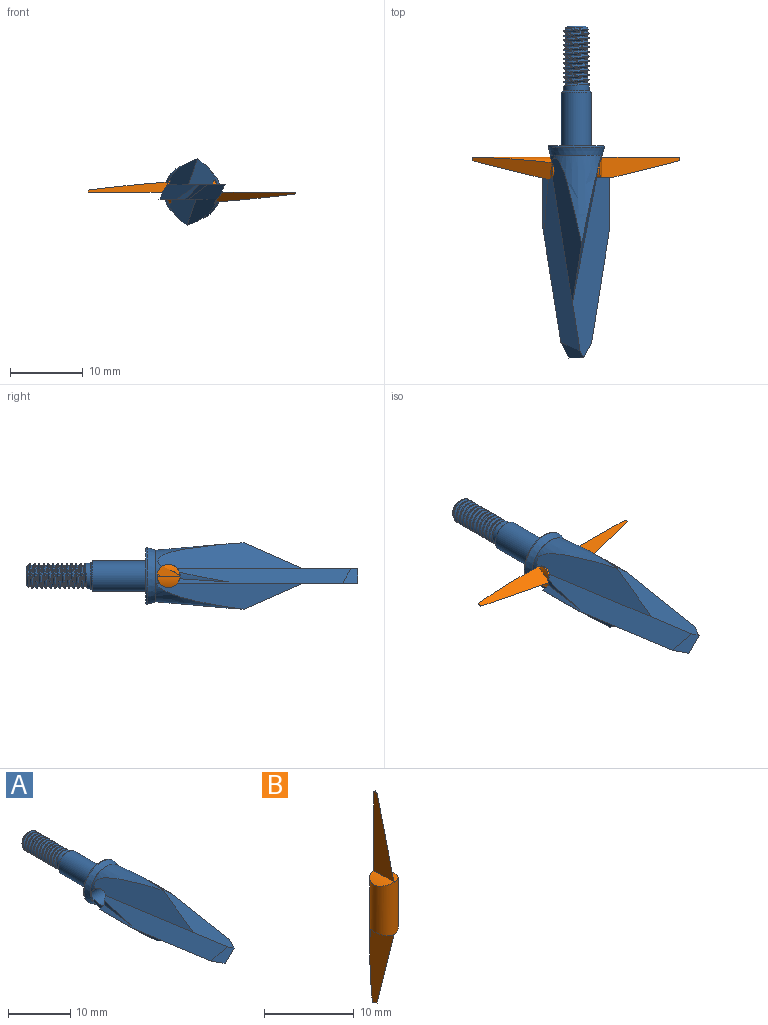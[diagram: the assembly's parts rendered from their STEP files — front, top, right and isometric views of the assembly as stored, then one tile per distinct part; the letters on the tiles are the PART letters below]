
ASSEMBLY  parts=2 mates=1
PART A: 55 faces, bbox 9.9x277.6x9.9 mm
  f0: plane 7.09x0.01mm, normal (-1,0,0), area 0.1mm2, adj f1,f2,f8,f33
  f1: plane 7.06x0.78mm, normal (-0.64,0,0.77), area 4.4mm2, adj f0,f2,f3,f33
  f2: cylinder r=1.59mm len=9.18mm, axis (-1,0,0), area 67.2mm2, adj f0,f1,f3,f4,f8,f9,f10,f11
  f3: cone r=3.56mm half-angle=5deg, axis (0,-1,0), area 3.2mm2, adj f1,f2,f33
  f4: plane 19.93x4.12mm, normal (0.81,-0.13,-0.57), area 58.8mm2, adj f2,f13,f26,f27,f28,f29,f32,f53
  f5: cylinder r=2.08mm len=7.37mm, axis (0,-1,0), area 96.4mm2, adj f7,f19
  f6: plane 3.66x3.66mm, normal (0,1,0), area 0.9mm2, adj f7,f34
  f7: cone r=1.83mm half-angle=45deg, axis (0,-1,0), area 4.4mm2, adj f5,f6
  f8: plane 24.87x5.12mm, normal (0,0,-1), area 67.9mm2, adj f0,f2,f29,f30,f31,f32,f33
  f9: plane 24.87x5.12mm, normal (0,0,1), area 67.9mm2, adj f2,f10,f25,f30,f31,f32,f33
  f10: plane 7.09x0.01mm, normal (1,0,0), area 0.1mm2, adj f2,f9,f11,f32
  f11: plane 7.06x0.78mm, normal (0.64,0,-0.77), area 4.4mm2, adj f2,f10,f16,f32
  f12: plane 0.63x0.18mm, normal (0,0,-1), area 0.1mm2, adj f2,f15,f29
  f13: cone r=3.56mm half-angle=5deg, axis (0,-1,0), area 38.6mm2, adj f2,f4,f14,f17,f26,f27,f29
  f14: plane 0.63x0.18mm, normal (0,0,1), area 0.1mm2, adj f2,f13,f25
  f15: cone r=3.56mm half-angle=5deg, axis (0,-1,0), area 38.6mm2, adj f2,f12,f17,f21,f23,f24,f25
  f16: cone r=3.56mm half-angle=5deg, axis (0,-1,0), area 3.2mm2, adj f2,f11,f32
  f17: plane 7.15x7.15mm, normal (0,-1,0), area 0.4mm2, adj f13,f15,f18
  f18: cone r=3.94mm half-angle=16deg, axis (0,1,0), area 27mm2, adj f17,f20
  f19: plane 7.54x7.54mm, normal (0,1,0), area 31mm2, adj f5,f20
  f20: torus R=3.77mm, axis (0,1,0), area 5.7mm2, adj f18,f19
  f21: plane 19.93x4.12mm, normal (-0.81,-0.13,0.57), area 58.8mm2, adj f2,f15,f22,f23,f24,f25,f33
  f22: bspline ~259.18x0.4mm, area 0mm2, adj f21,f23,f24
  f23: plane 0.04x0.03mm, normal (0,-1,0), area 0mm2, adj f15,f21,f22,f24
  f24: bspline ~259.18x0.42mm, area 0mm2, adj f15,f21,f22,f23
  f25: plane 20.32x3.94mm, normal (0.98,-0.19,0.09), area 43.2mm2, adj f2,f9,f14,f15,f21
  f26: plane 0.04x0.03mm, normal (0,-1,0), area 0mm2, adj f4,f13,f27,f28
  f27: bspline ~259.18x0.42mm, area 0mm2, adj f4,f13,f26,f28
  f28: bspline ~259.18x0.4mm, area 0mm2, adj f4,f26,f27
  f29: plane 20.32x3.94mm, normal (-0.98,-0.19,-0.09), area 43.2mm2, adj f2,f4,f8,f12,f13
  f30: plane 3.13x2.14mm, normal (-0.66,-0.34,0.66), area 4.7mm2, adj f8,f9,f31,f33
  f31: plane 3.13x2.14mm, normal (0.66,-0.34,-0.66), area 4.7mm2, adj f8,f9,f30,f32
  f32: plane 24.57x5.77mm, normal (0.63,-0.1,-0.77), area 65mm2, adj f2,f4,f8,f9,f10,f11,f16,f31
  f33: plane 24.57x5.77mm, normal (-0.63,-0.1,0.77), area 65mm2, adj f0,f1,f2,f3,f8,f9,f21,f30
  f34: cylinder r=1.75mm len=3.51mm, axis (0,-1,0), area 7.4mm2, adj f6,f35,f49,f50,f52
  f35: cylinder r=1.75mm len=3.51mm, axis (0,-1,0), area 1mm2, adj f34,f36,f50,f52
  f36: cylinder r=1.75mm len=3.51mm, axis (0,-1,0), area 1mm2, adj f35,f37,f50,f52
  f37: cylinder r=1.75mm len=3.51mm, axis (0,-1,0), area 1mm2, adj f36,f38,f50,f52
  f38: cylinder r=1.75mm len=3.51mm, axis (0,-1,0), area 1mm2, adj f37,f39,f50,f52
  f39: cylinder r=1.75mm len=3.51mm, axis (0,-1,0), area 1mm2, adj f38,f40,f50,f52
  f40: cylinder r=1.75mm len=3.51mm, axis (0,-1,0), area 1mm2, adj f39,f41,f50,f52
  f41: cylinder r=1.75mm len=3.51mm, axis (0,-1,0), area 1mm2, adj f40,f42,f50,f52
  f42: cylinder r=1.75mm len=3.51mm, axis (0,-1,0), area 1mm2, adj f41,f43,f50,f52
  f43: cylinder r=1.75mm len=3.51mm, axis (0,-1,0), area 1mm2, adj f42,f44,f50,f52
  f44: cylinder r=1.75mm len=3.51mm, axis (0,-1,0), area 1mm2, adj f43,f45,f50,f52
  f45: cylinder r=1.75mm len=3.51mm, axis (0,-1,0), area 1mm2, adj f44,f46,f50,f52
  f46: cylinder r=1.75mm len=1.33mm, axis (0,-1,0), area 0.1mm2, adj f45,f48,f52
  f47: plane 2.49x2.49mm, normal (0,1,0), area 4.9mm2, adj f48
  f48: cone r=1.24mm half-angle=45deg, axis (0,-1,0), area 4.6mm2, adj f46,f47,f50,f51,f52
  f49: plane 0.55x0.27mm, normal (0,0,-1), area 0.1mm2, adj f34,f50,f51,f52
  f50: bspline ~8.47x4.05mm, area 45.1mm2, adj f34,f35,f36,f37,f38,f39,f40,f41
  f51: cylinder r=1.48mm len=8.16mm, axis (0,1,0), area 20.7mm2, adj f48,f49,f50,f52
  f52: bspline ~8.23x4.05mm, area 41.3mm2, adj f34,f35,f36,f37,f38,f39,f40,f41
  f53: plane 0.62x0.11mm, normal (0.75,-0.14,0.64), area 0mm2, adj f4,f32,f54
  f54: plane 0.01x0.01mm, normal (0,0.99,-0.13), area 0mm2, adj f4,f32,f53
PART B: 13 faces, bbox 3.3x3.3x28.7 mm
  f0: cylinder r=1.59mm len=28.58mm, axis (0,0,-1), area 87.8mm2, adj f1,f2,f3,f4,f6,f7,f8,f9
  f1: cylinder r=3.56mm len=2.38mm, axis (0,1,0), area 1.6mm2, adj f0,f5,f9,f12
  f2: plane 10.73x3.18mm, normal (-1,0,0), area 19.8mm2, adj f0,f4,f7,f11
  f3: cylinder r=3.56mm len=3.18mm, axis (0,1,0), area 4.1mm2, adj f0,f6
  f4: plane 11.09x3.24mm, normal (0.87,-0.49,0.12), area 19.3mm2, adj f0,f2,f8,f11
  f5: plane 0.07x0.04mm, normal (-0.5,0.86,0.12), area 0mm2, adj f1,f9,f12
  f6: plane 10.73x3.18mm, normal (1,0,0), area 19.8mm2, adj f0,f3,f9,f10
  f7: cylinder r=3.56mm len=3.18mm, axis (0,1,0), area 4.1mm2, adj f0,f2
  f8: cylinder r=3.56mm len=2.38mm, axis (0,1,0), area 1.6mm2, adj f0,f4
  f9: plane 11.03x3.17mm, normal (-0.87,-0.49,-0.12), area 19.3mm2, adj f0,f1,f5,f6,f10,f12
  f10: plane 0.51x0.27mm, normal (0,0,-1), area 0.1mm2, adj f0,f6,f9
  f11: plane 0.51x0.27mm, normal (0,0,1), area 0.1mm2, adj f0,f2,f4
  f12: plane 1.08x0.59mm, normal (0.08,0.11,-0.99), area 0.1mm2, adj f1,f5,f9
PLACE A at identity fixed
PLACE B rot(axis=(0,1,0),90deg) t=(-0.04,8.31,0)mm
MATE cylindrical B.f0 <-> A.f2  axis (-1,0,0) through (-0.04,8.31,0)mm
